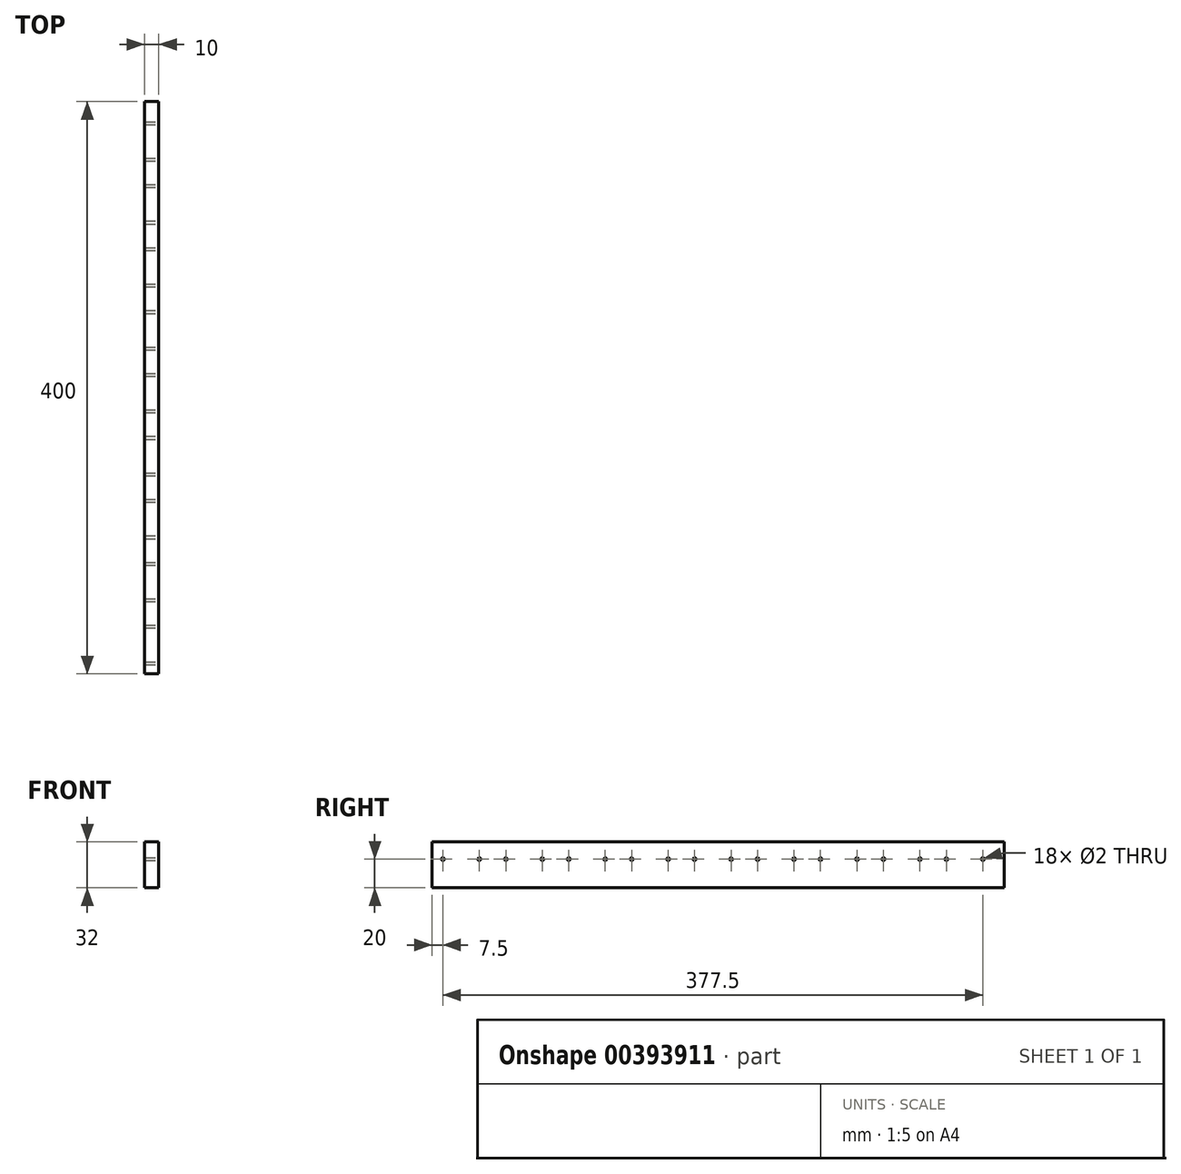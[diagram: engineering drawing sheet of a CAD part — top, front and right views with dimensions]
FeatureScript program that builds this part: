
annotation { "Feature Type Name" : "Feature", "Feature Type Description" : "" }
export const myFeature = defineFeature(function(context is Context, id is Id, definition is map)
    precondition{}
    {
        {
            var Q0;
            Q0=qCreatedBy(makeId("Right.planeOp"),FACE);
            var sketch = newSketch(context, id + "F0", { "sketchPlane" : qUnion([Q0])});
            skLineSegment(sketch, "E0.bottom", {"start": v(200, 16) * mm, "end": v(-200, 16) * mm});
            skLineSegment(sketch, "E0.top", {"start": v(200, -16) * mm, "end": v(-200, -16) * mm});
            skLineSegment(sketch, "E0.left", {"start": v(200, 16) * mm, "end": v(200, -16) * mm});
            skLineSegment(sketch, "E0.right", {"start": v(-200, 16) * mm, "end": v(-200, -16) * mm});
            skPoint(sketch, "E0.middle", {"position": v(0, 0) * mm});
            skSolve(sketch);
        }
        {
            var Q0;
            Q0=makeQuery(id+"F0.imprint","IMPRINT",FACE,{"disambiguationData":[TD([[makeQuery(id+"F0.imprint","IMPRINT",EDGE,{"derivedFrom":sQuery(id+"F0.wireOp",EDGE,"E0.bottom")}),1.0]])]});
            extrude(context, id + "F1", {"entities" : qUnion([Q0]), "depth" : 10 * mm});
        }
        {
            var Q0;
            Q0=makeQuery(id+"F1.opExtrude","CAP_FACE",FACE,{"disambiguationData":[OSD([sQuery(id+"F0.wireOp",EDGE,"E0.bottom"),sQuery(id+"F0.wireOp",EDGE,"E0.top"),sQuery(id+"F0.wireOp",EDGE,"E0.left"),sQuery(id+"F0.wireOp",EDGE,"E0.right")])],"isStart":false});
            var sketch = newSketch(context, id + "F2", { "sketchPlane" : qUnion([Q0])});
            skLineSegment(sketch, "E1", {"start": v(-200, 4) * mm, "end": v(200, 4) * mm, "construction": true});
            skCircle(sketch, "E2", {"center": v(-79, 4) * mm, "radius": 1 * mm});
            skCircle(sketch, "E3", {"center": v(-104.5, 4) * mm, "radius": 1 * mm});
            skCircle(sketch, "E4", {"center": v(-123, 4) * mm, "radius": 1 * mm});
            skCircle(sketch, "E5", {"center": v(-148.5, 4) * mm, "radius": 1 * mm});
            skCircle(sketch, "E6", {"center": v(-167, 4) * mm, "radius": 1 * mm});
            skCircle(sketch, "E7", {"center": v(-192.5, 4) * mm, "radius": 1 * mm});
            skCircle(sketch, "E8", {"center": v(-60.5, 4) * mm, "radius": 1 * mm});
            skCircle(sketch, "E9", {"center": v(-35, 4) * mm, "radius": 1 * mm});
            skCircle(sketch, "E10", {"center": v(-16.5, 4) * mm, "radius": 1 * mm});
            skCircle(sketch, "E11", {"center": v(9, 4) * mm, "radius": 1 * mm});
            skCircle(sketch, "E12", {"center": v(27.5, 4) * mm, "radius": 1 * mm});
            skCircle(sketch, "E13", {"center": v(53, 4) * mm, "radius": 1 * mm});
            skCircle(sketch, "E14", {"center": v(71.5, 4) * mm, "radius": 1 * mm});
            skCircle(sketch, "E15", {"center": v(97, 4) * mm, "radius": 1 * mm});
            skCircle(sketch, "E16", {"center": v(115.5, 4) * mm, "radius": 1 * mm});
            skCircle(sketch, "E17", {"center": v(141, 4) * mm, "radius": 1 * mm});
            skCircle(sketch, "E18", {"center": v(159.5, 4) * mm, "radius": 1 * mm});
            skCircle(sketch, "E19", {"center": v(145.02, 4) * mm, "radius": 1 * mm});
            skCircle(sketch, "E20", {"center": v(185, 4) * mm, "radius": 1 * mm});
            skSolve(sketch);
        }
        {
            var Q0;
            Q0=makeQuery(id+"F2.imprint","IMPRINT",FACE,{"disambiguationData":[TD([[makeQuery(id+"F2.imprint","IMPRINT",EDGE,{"derivedFrom":sQuery(id+"F2.wireOp",EDGE,"E7")}),1.0]])]});
            var Q1;
            Q1=makeQuery(id+"F2.imprint","IMPRINT",FACE,{"disambiguationData":[TD([[makeQuery(id+"F2.imprint","IMPRINT",EDGE,{"derivedFrom":sQuery(id+"F2.wireOp",EDGE,"E6")}),1.0]])]});
            var Q2;
            Q2=makeQuery(id+"F2.imprint","IMPRINT",FACE,{"disambiguationData":[TD([[makeQuery(id+"F2.imprint","IMPRINT",EDGE,{"derivedFrom":sQuery(id+"F2.wireOp",EDGE,"E5")}),1.0]])]});
            var Q3;
            Q3=makeQuery(id+"F2.imprint","IMPRINT",FACE,{"disambiguationData":[TD([[makeQuery(id+"F2.imprint","IMPRINT",EDGE,{"derivedFrom":sQuery(id+"F2.wireOp",EDGE,"E4")}),1.0]])]});
            var Q4;
            Q4=makeQuery(id+"F2.imprint","IMPRINT",FACE,{"disambiguationData":[TD([[makeQuery(id+"F2.imprint","IMPRINT",EDGE,{"derivedFrom":sQuery(id+"F2.wireOp",EDGE,"E3")}),1.0]])]});
            var Q5;
            Q5=makeQuery(id+"F2.imprint","IMPRINT",FACE,{"disambiguationData":[TD([[makeQuery(id+"F2.imprint","IMPRINT",EDGE,{"derivedFrom":sQuery(id+"F2.wireOp",EDGE,"E2")}),1.0]])]});
            var Q6;
            Q6=makeQuery(id+"F2.imprint","IMPRINT",FACE,{"disambiguationData":[TD([[makeQuery(id+"F2.imprint","IMPRINT",EDGE,{"derivedFrom":sQuery(id+"F2.wireOp",EDGE,"E8")}),1.0]])]});
            var Q7;
            Q7=makeQuery(id+"F2.imprint","IMPRINT",FACE,{"disambiguationData":[TD([[makeQuery(id+"F2.imprint","IMPRINT",EDGE,{"derivedFrom":sQuery(id+"F2.wireOp",EDGE,"E9")}),1.0]])]});
            var Q8;
            Q8=makeQuery(id+"F2.imprint","IMPRINT",FACE,{"disambiguationData":[TD([[makeQuery(id+"F2.imprint","IMPRINT",EDGE,{"derivedFrom":sQuery(id+"F2.wireOp",EDGE,"E10")}),1.0]])]});
            var Q9;
            Q9=makeQuery(id+"F2.imprint","IMPRINT",FACE,{"disambiguationData":[TD([[makeQuery(id+"F2.imprint","IMPRINT",EDGE,{"derivedFrom":sQuery(id+"F2.wireOp",EDGE,"E11")}),1.0]])]});
            var Q10;
            Q10=makeQuery(id+"F2.imprint","IMPRINT",FACE,{"disambiguationData":[TD([[makeQuery(id+"F2.imprint","IMPRINT",EDGE,{"derivedFrom":sQuery(id+"F2.wireOp",EDGE,"E12")}),1.0]])]});
            var Q11;
            Q11=makeQuery(id+"F2.imprint","IMPRINT",FACE,{"disambiguationData":[TD([[makeQuery(id+"F2.imprint","IMPRINT",EDGE,{"derivedFrom":sQuery(id+"F2.wireOp",EDGE,"E13")}),1.0]])]});
            var Q12;
            Q12=makeQuery(id+"F2.imprint","IMPRINT",FACE,{"disambiguationData":[TD([[makeQuery(id+"F2.imprint","IMPRINT",EDGE,{"derivedFrom":sQuery(id+"F2.wireOp",EDGE,"E14")}),1.0]])]});
            var Q13;
            Q13=makeQuery(id+"F2.imprint","IMPRINT",FACE,{"disambiguationData":[TD([[makeQuery(id+"F2.imprint","IMPRINT",EDGE,{"derivedFrom":sQuery(id+"F2.wireOp",EDGE,"E15")}),1.0]])]});
            var Q14;
            Q14=makeQuery(id+"F2.imprint","IMPRINT",FACE,{"disambiguationData":[TD([[makeQuery(id+"F2.imprint","IMPRINT",EDGE,{"derivedFrom":sQuery(id+"F2.wireOp",EDGE,"E16")}),1.0]])]});
            var Q15;
            {var subQ0=sQuery(id+"F2.wireOp",EDGE,"E19");var subQ1=sQuery(id+"F2.wireOp",EDGE,"E17");var subQ2=makeQuery(id+"F2.imprint","INTERSECT",VERTEX,{"disambiguationData":[OD(0.0)],"derivedFrom":[subQ1,subQ0]});Q15=makeQuery(id+"F2.imprint","IMPRINT",FACE,{"disambiguationData":[TD([[makeQuery(id+"F2.imprint","IMPRINT",EDGE,{"disambiguationData":[TD([[subQ2,-1.0]])],"derivedFrom":subQ1}),1.0]])]});}
            var Q16;
            Q16=makeQuery(id+"F2.imprint","IMPRINT",FACE,{"disambiguationData":[TD([[makeQuery(id+"F2.imprint","IMPRINT",EDGE,{"derivedFrom":sQuery(id+"F2.wireOp",EDGE,"E18")}),1.0]])]});
            var Q17;
            Q17=makeQuery(id+"F2.imprint","IMPRINT",FACE,{"disambiguationData":[TD([[makeQuery(id+"F2.imprint","IMPRINT",EDGE,{"derivedFrom":sQuery(id+"F2.wireOp",EDGE,"E20")}),1.0]])]});
            extrude(context, id + "F3", {"entities" : qUnion([Q0, Q1, Q2, Q3, Q4, Q5, Q6, Q7, Q8, Q9, Q10, Q11, Q12, Q13, Q14, Q15, Q16, Q17]), "operationType" : NewBodyOperationType.REMOVE, "oppositeDirection" : true, "depth" : 25 * mm});
        }
    });
